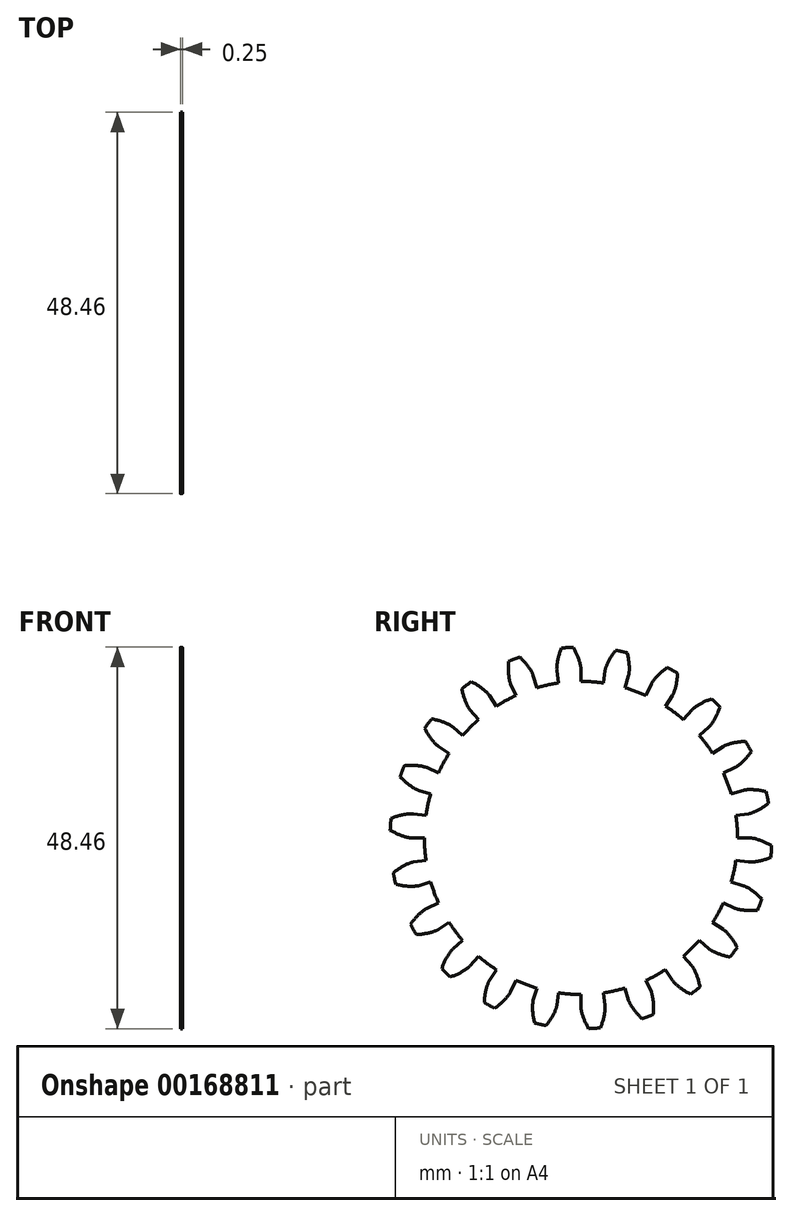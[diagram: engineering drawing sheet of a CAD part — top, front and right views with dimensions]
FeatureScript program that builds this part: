
annotation { "Feature Type Name" : "Feature", "Feature Type Description" : "" }
export const myFeature = defineFeature(function(context is Context, id is Id, definition is map)
    precondition{}
    {
        {
            assignVariable(context, id + "F0", {"name" : "NumberTeeth", "anyValue" : 22});
        }
        {
            assignVariable(context, id + "F1", {"name" : "GearThickness", "anyValue" : 0.25});
        }
        {
            var Q0;
            Q0=qCreatedBy(makeId("Right.planeOp"),FACE);
            var sketch = newSketch(context, id + "F2", { "sketchPlane" : qUnion([Q0])});
            skCircle(sketch, "E0", {"center": v(0, 0) * mm, "radius": 19.89 * mm});
            skCircle(sketch, "E1", {"center": v(0, 0) * mm, "radius": 21.52 * mm, "construction": true});
            skCircle(sketch, "E2", {"center": v(0, 0) * mm, "radius": 22.22 * mm, "construction": true});
            skCircle(sketch, "E3", {"center": v(0, 0) * mm, "radius": 24.25 * mm});
            skLineSegment(sketch, "E4", {"start": v(0, 0) * mm, "end": v(-21.52, 0) * mm, "construction": true});
            skLineSegment(sketch, "E5.1.0", {"start": v(0, 0) * mm, "end": v(-21.5, 1.08) * mm, "construction": true});
            skLineSegment(sketch, "E5.2.0", {"start": v(0, 0) * mm, "end": v(-21.4, 2.15) * mm, "construction": true});
            skLineSegment(sketch, "E5.3.0", {"start": v(0, 0) * mm, "end": v(-21.28, 3.22) * mm, "construction": true});
            skLineSegment(sketch, "E5.4.0", {"start": v(0, 0) * mm, "end": v(-21.09, 4.27) * mm, "construction": true});
            skLineSegment(sketch, "E5.5.0", {"start": v(0, 0) * mm, "end": v(-20.85, 5.32) * mm, "construction": true});
            skLineSegment(sketch, "E5.6.0", {"start": v(0, 0) * mm, "end": v(-20.56, 6.36) * mm, "construction": true});
            skLineSegment(sketch, "E5.7.0", {"start": v(0, 0) * mm, "end": v(-20.21, 7.38) * mm, "construction": true});
            skLineSegment(sketch, "E5.8.0", {"start": v(0, 0) * mm, "end": v(-19.82, 8.38) * mm, "construction": true});
            skLineSegment(sketch, "E5.9.0", {"start": v(0, 0) * mm, "end": v(-19.37, 9.36) * mm, "construction": true});
            skLineSegment(sketch, "E5.10.0", {"start": v(0, 0) * mm, "end": v(-18.88, 10.32) * mm, "construction": true});
            skLineSegment(sketch, "E5.11.0", {"start": v(0, 0) * mm, "end": v(-18.34, 11.25) * mm, "construction": true});
            skLineSegment(sketch, "E5.12.0", {"start": v(0, 0) * mm, "end": v(-17.76, 12.15) * mm, "construction": true});
            skLineSegment(sketch, "E5.13.0", {"start": v(0, 0) * mm, "end": v(-17.13, 13.02) * mm, "construction": true});
            skLineSegment(sketch, "E5.14.0", {"start": v(0, 0) * mm, "end": v(-16.46, 13.86) * mm, "construction": true});
            skLineSegment(sketch, "E5.anchor2", {"start": v(0, 0) * mm, "end": v(-16.46, 13.86) * mm, "construction": true});
            skLineSegment(sketch, "E6", {"start": v(-21.5, 1.08) * mm, "end": v(-21.54, 0) * mm, "construction": true});
            skLineSegment(sketch, "E7", {"start": v(-21.4, 2.15) * mm, "end": v(-21.62, 0) * mm, "construction": true});
            skLineSegment(sketch, "E8", {"start": v(-21.28, 3.22) * mm, "end": v(-21.76, 0.02) * mm, "construction": true});
            skLineSegment(sketch, "E9", {"start": v(-20.85, 5.32) * mm, "end": v(-22.18, 0.11) * mm, "construction": true});
            skLineSegment(sketch, "E10", {"start": v(-20.56, 6.36) * mm, "end": v(-22.46, 0.2) * mm, "construction": true});
            skLineSegment(sketch, "E11", {"start": v(-20.21, 7.38) * mm, "end": v(-22.8, 0.3) * mm, "construction": true});
            skLineSegment(sketch, "E12", {"start": v(-19.82, 8.38) * mm, "end": v(-23.17, 0.45) * mm, "construction": true});
            skLineSegment(sketch, "E13", {"start": v(-19.37, 9.36) * mm, "end": v(-23.59, 0.64) * mm, "construction": true});
            skLineSegment(sketch, "E14", {"start": v(-18.88, 10.32) * mm, "end": v(-24.04, 0.87) * mm, "construction": true});
            skLineSegment(sketch, "E15", {"start": v(-18.34, 11.25) * mm, "end": v(-24.53, 1.16) * mm, "construction": true});
            skLineSegment(sketch, "E16", {"start": v(-21.09, 4.27) * mm, "end": v(-21.94, 0.06) * mm, "construction": true});
            skLineSegment(sketch, "E17", {"start": v(-17.76, 12.15) * mm, "end": v(-25.05, 1.5) * mm, "construction": true});
            skLineSegment(sketch, "E18", {"start": v(-17.13, 13.02) * mm, "end": v(-25.6, 1.89) * mm, "construction": true});
            skLineSegment(sketch, "E19", {"start": v(-16.46, 13.86) * mm, "end": v(-26.16, 2.34) * mm, "construction": true});
            skLineSegment(sketch, "E20", {"start": v(0, 0) * mm, "end": v(-21.46, 1.54) * mm, "construction": true});
            skLineSegment(sketch, "E21", {"start": v(-19.89, 0) * mm, "end": v(-21.52, 0) * mm});
            skLineSegment(sketch, "E22.MirrorCS", {"start": v(-19.68, 2.83) * mm, "end": v(-21.3, 3.06) * mm});
            skFitSpline(sketch, "E23", {"points": [v(-21.52, 0) * mm, v(-21.54, 0) * mm, v(-21.62, 0) * mm, v(-21.76, 0.02) * mm, v(-21.94, 0.06) * mm, v(-22.18, 0.11) * mm, v(-22.46, 0.2) * mm, v(-22.8, 0.3) * mm, v(-23.17, 0.45) * mm, v(-23.59, 0.64) * mm, v(-24.04, 0.87) * mm, v(-24.53, 1.16) * mm, v(-25.05, 1.5) * mm, v(-25.6, 1.89) * mm, v(-26.16, 2.34) * mm], "startDerivative": vector(-0.77, 0) * mm, "endDerivative": vector(-1.36, 1.15) * mm});
            skLineSegment(sketch, "E24", {"start": v(-21.81, -1.32) * mm, "end": v(-26.16, 2.34) * mm, "construction": true});
            skFitSpline(sketch, "E25.MirrorCS", {"points": [v(-21.3, 3.06) * mm, v(-21.32, 3.07) * mm, v(-21.4, 3.07) * mm, v(-21.54, 3.07) * mm, v(-21.73, 3.07) * mm, v(-21.97, 3.05) * mm, v(-22.26, 3) * mm, v(-22.6, 2.94) * mm, v(-23, 2.85) * mm, v(-23.44, 2.72) * mm, v(-23.92, 2.56) * mm, v(-24.44, 2.35) * mm, v(-25, 2.09) * mm, v(-25.6, 1.77) * mm, v(-26.23, 1.4) * mm], "startDerivative": vector(-0.77, 0.11) * mm, "endDerivative": vector(-1.51, -0.94) * mm});
            skSolve(sketch);
        }
        {
            var Q0;
            {var subQ0=sQuery(id+"F2.wireOp",EDGE,"E0");var subQ27=makeQuery(id+"F2.imprint","INTERSECT",VERTEX,{"derivedFrom":[subQ0,sQuery(id+"F2.wireOp",EDGE,"10ea1024-8cf5-41f5-a75f-a634b86921f3.10.0")]});Q0=makeQuery(id+"F2.imprint","IMPRINT",FACE,{"disambiguationData":[TD([[makeQuery(id+"F2.imprint","IMPRINT",EDGE,{"disambiguationData":[TD([[subQ27,-1.0]])],"derivedFrom":subQ0}),1.0]])]});}
            var Q1;
            {var subQ0=sQuery(id+"F2.wireOp",EDGE,"10ea1024-8cf5-41f5-a75f-a634b86921f3.1.0");Q1=makeQuery(id+"F2.imprint","IMPRINT",FACE,{"disambiguationData":[TD([[makeQuery(id+"F2.imprint","IMPRINT",EDGE,{"derivedFrom":subQ0}),-1.0]])]});}
            var Q2;
            {var subQ7=sQuery(id+"F2.wireOp",EDGE,"10ea1024-8cf5-41f5-a75f-a634b86921f3.2.0");Q2=makeQuery(id+"F2.imprint","IMPRINT",FACE,{"disambiguationData":[TD([[makeQuery(id+"F2.imprint","IMPRINT",EDGE,{"derivedFrom":subQ7}),-1.0]])]});}
            var Q3;
            {var subQ8=sQuery(id+"F2.wireOp",EDGE,"10ea1024-8cf5-41f5-a75f-a634b86921f3.3.0");Q3=makeQuery(id+"F2.imprint","IMPRINT",FACE,{"disambiguationData":[TD([[makeQuery(id+"F2.imprint","IMPRINT",EDGE,{"derivedFrom":subQ8}),-1.0]])]});}
            var Q4;
            {var subQ2=sQuery(id+"F2.wireOp",EDGE,"10ea1024-8cf5-41f5-a75f-a634b86921f3.4.0");Q4=makeQuery(id+"F2.imprint","IMPRINT",FACE,{"disambiguationData":[TD([[makeQuery(id+"F2.imprint","IMPRINT",EDGE,{"derivedFrom":subQ2}),-1.0]])]});}
            var Q5;
            {var subQ8=sQuery(id+"F2.wireOp",EDGE,"10ea1024-8cf5-41f5-a75f-a634b86921f3.5.0");Q5=makeQuery(id+"F2.imprint","IMPRINT",FACE,{"disambiguationData":[TD([[makeQuery(id+"F2.imprint","IMPRINT",EDGE,{"derivedFrom":subQ8}),-1.0]])]});}
            var Q6;
            {var subQ3=sQuery(id+"F2.wireOp",EDGE,"10ea1024-8cf5-41f5-a75f-a634b86921f3.6.0");Q6=makeQuery(id+"F2.imprint","IMPRINT",FACE,{"disambiguationData":[TD([[makeQuery(id+"F2.imprint","IMPRINT",EDGE,{"derivedFrom":subQ3}),-1.0]])]});}
            var Q7;
            {var subQ0=sQuery(id+"F2.wireOp",EDGE,"10ea1024-8cf5-41f5-a75f-a634b86921f3.7.0");Q7=makeQuery(id+"F2.imprint","IMPRINT",FACE,{"disambiguationData":[TD([[makeQuery(id+"F2.imprint","IMPRINT",EDGE,{"derivedFrom":subQ0}),-1.0]])]});}
            var Q8;
            {var subQ5=sQuery(id+"F2.wireOp",EDGE,"10ea1024-8cf5-41f5-a75f-a634b86921f3.8.0");Q8=makeQuery(id+"F2.imprint","IMPRINT",FACE,{"disambiguationData":[TD([[makeQuery(id+"F2.imprint","IMPRINT",EDGE,{"derivedFrom":subQ5}),-1.0]])]});}
            var Q9;
            {var subQ1=sQuery(id+"F2.wireOp",EDGE,"10ea1024-8cf5-41f5-a75f-a634b86921f3.9.0");Q9=makeQuery(id+"F2.imprint","IMPRINT",FACE,{"disambiguationData":[TD([[makeQuery(id+"F2.imprint","IMPRINT",EDGE,{"derivedFrom":subQ1}),-1.0]])]});}
            var Q10;
            {var subQ5=sQuery(id+"F2.wireOp",EDGE,"10ea1024-8cf5-41f5-a75f-a634b86921f3.10.0");Q10=makeQuery(id+"F2.imprint","IMPRINT",FACE,{"disambiguationData":[TD([[makeQuery(id+"F2.imprint","IMPRINT",EDGE,{"derivedFrom":subQ5}),-1.0]])]});}
            var Q11;
            {var subQ8=sQuery(id+"F2.wireOp",EDGE,"10ea1024-8cf5-41f5-a75f-a634b86921f3.11.0");Q11=makeQuery(id+"F2.imprint","IMPRINT",FACE,{"disambiguationData":[TD([[makeQuery(id+"F2.imprint","IMPRINT",EDGE,{"derivedFrom":subQ8}),-1.0]])]});}
            var Q12;
            {var subQ2=sQuery(id+"F2.wireOp",EDGE,"10ea1024-8cf5-41f5-a75f-a634b86921f3.12.0");Q12=makeQuery(id+"F2.imprint","IMPRINT",FACE,{"disambiguationData":[TD([[makeQuery(id+"F2.imprint","IMPRINT",EDGE,{"derivedFrom":subQ2}),-1.0]])]});}
            var Q13;
            {var subQ3=sQuery(id+"F2.wireOp",EDGE,"10ea1024-8cf5-41f5-a75f-a634b86921f3.13.0");Q13=makeQuery(id+"F2.imprint","IMPRINT",FACE,{"disambiguationData":[TD([[makeQuery(id+"F2.imprint","IMPRINT",EDGE,{"derivedFrom":subQ3}),-1.0]])]});}
            var Q14;
            {var subQ0=sQuery(id+"F2.wireOp",EDGE,"10ea1024-8cf5-41f5-a75f-a634b86921f3.14.0");Q14=makeQuery(id+"F2.imprint","IMPRINT",FACE,{"disambiguationData":[TD([[makeQuery(id+"F2.imprint","IMPRINT",EDGE,{"derivedFrom":subQ0}),-1.0]])]});}
            var Q15;
            {var subQ6=sQuery(id+"F2.wireOp",EDGE,"10ea1024-8cf5-41f5-a75f-a634b86921f3.15.0");Q15=makeQuery(id+"F2.imprint","IMPRINT",FACE,{"disambiguationData":[TD([[makeQuery(id+"F2.imprint","IMPRINT",EDGE,{"derivedFrom":subQ6}),-1.0]])]});}
            var Q16;
            {var subQ5=sQuery(id+"F2.wireOp",EDGE,"10ea1024-8cf5-41f5-a75f-a634b86921f3.16.0");Q16=makeQuery(id+"F2.imprint","IMPRINT",FACE,{"disambiguationData":[TD([[makeQuery(id+"F2.imprint","IMPRINT",EDGE,{"derivedFrom":subQ5}),-1.0]])]});}
            var Q17;
            {var subQ7=sQuery(id+"F2.wireOp",EDGE,"10ea1024-8cf5-41f5-a75f-a634b86921f3.17.0");Q17=makeQuery(id+"F2.imprint","IMPRINT",FACE,{"disambiguationData":[TD([[makeQuery(id+"F2.imprint","IMPRINT",EDGE,{"derivedFrom":subQ7}),-1.0]])]});}
            var Q18;
            {var subQ5=sQuery(id+"F2.wireOp",EDGE,"10ea1024-8cf5-41f5-a75f-a634b86921f3.18.0");Q18=makeQuery(id+"F2.imprint","IMPRINT",FACE,{"disambiguationData":[TD([[makeQuery(id+"F2.imprint","IMPRINT",EDGE,{"derivedFrom":subQ5}),-1.0]])]});}
            var Q19;
            {var subQ8=sQuery(id+"F2.wireOp",EDGE,"10ea1024-8cf5-41f5-a75f-a634b86921f3.19.0");Q19=makeQuery(id+"F2.imprint","IMPRINT",FACE,{"disambiguationData":[TD([[makeQuery(id+"F2.imprint","IMPRINT",EDGE,{"derivedFrom":subQ8}),-1.0]])]});}
            var Q20;
            {var subQ8=sQuery(id+"F2.wireOp",EDGE,"E21");Q20=makeQuery(id+"F2.imprint","IMPRINT",FACE,{"disambiguationData":[TD([[makeQuery(id+"F2.imprint","IMPRINT",EDGE,{"derivedFrom":subQ8}),-1.0]])]});}
            extrude(context, id + "F3", {"entities" : qUnion([Q0, Q1, Q2, Q3, Q4, Q5, Q6, Q7, Q8, Q9, Q10, Q11, Q12, Q13, Q14, Q15, Q16, Q17, Q18, Q19, Q20]), "depth" : (getVariable(context, 'GearThickness')) * mm});
        }
        {
            var Q0;
            Q0=makeQuery(id+"F3.opExtrude","SWEPT_FACE",FACE,{"disambiguationData":[OSD([sQuery(id+"F2.wireOp",EDGE,"E25.MirrorCS")])]});
            var Q1;
            Q1=makeQuery(id+"F3.opExtrude","SWEPT_FACE",FACE,{"disambiguationData":[OSD([sQuery(id+"F2.wireOp",EDGE,"E23")])]});
            var Q2;
            Q2=makeQuery(id+"F3.opExtrude","SWEPT_FACE",FACE,{"disambiguationData":[OSD([sQuery(id+"F2.wireOp",EDGE,"E3")])]});
            var Q3;
            Q3=makeQuery(id+"F3.opExtrude","SWEPT_FACE",FACE,{"disambiguationData":[OSD([sQuery(id+"F2.wireOp",EDGE,"E22.MirrorCS")])]});
            var Q4;
            Q4=makeQuery(id+"F3.opExtrude","SWEPT_FACE",FACE,{"disambiguationData":[OSD([sQuery(id+"F2.wireOp",EDGE,"E21")])]});
            var Q5;
            Q5=makeQuery(id+"F3.opExtrude","SWEPT_FACE",FACE,{"disambiguationData":[OSD([sQuery(id+"F2.wireOp",EDGE,"E0")])]});
            circularPattern(context, id + "F4", {"faces" : qUnion([Q0, Q1, Q2, Q3, Q4]), "axis" : qUnion([Q5]), "angle" : 360 * degree, "instanceCount" : getVariable(context, 'NumberTeeth'), "equalSpace" : true, "patternType" : PatternType.FACE});
        }
    });
